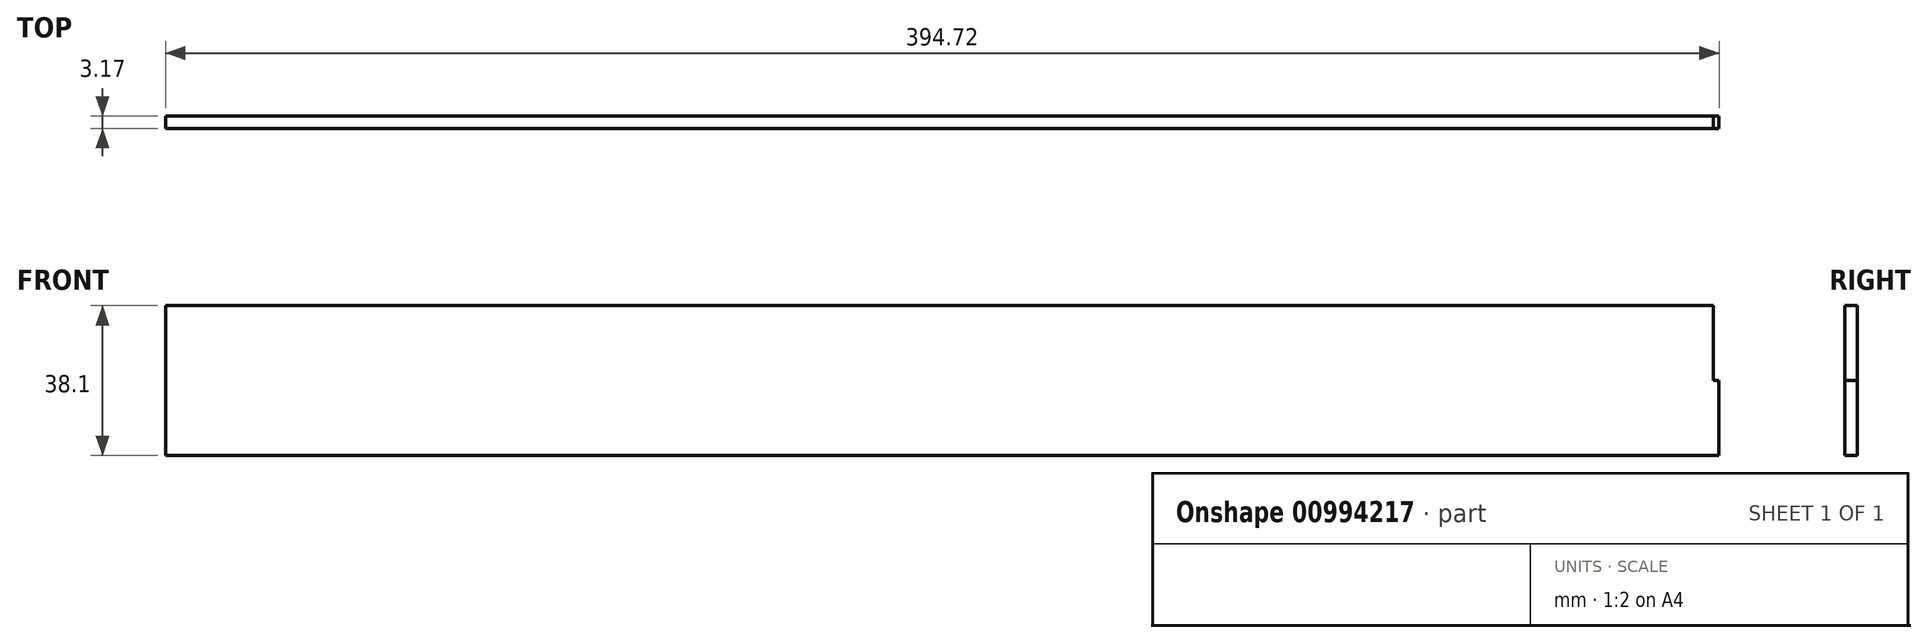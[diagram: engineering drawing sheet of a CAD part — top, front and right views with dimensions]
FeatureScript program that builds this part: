
annotation { "Feature Type Name" : "Feature", "Feature Type Description" : "" }
export const myFeature = defineFeature(function(context is Context, id is Id, definition is map)
    precondition{}
    {
        {
            var Q0;
            Q0=qCreatedBy(makeId("Front.planeOp"),FACE);
            var sketch = newSketch(context, id + "F0", { "sketchPlane" : qUnion([Q0])});
            skLineSegment(sketch, "E0", {"start": v(0, 0) * mm, "end": v(0, 38.1) * mm});
            skLineSegment(sketch, "E1", {"start": v(0, 38.1) * mm, "end": v(393.2, 38.1) * mm});
            skLineSegment(sketch, "E2", {"start": v(393.2, 38.1) * mm, "end": v(393.2, 19.05) * mm});
            skLineSegment(sketch, "E3", {"start": v(0, 0) * mm, "end": v(394.72, 0) * mm});
            skLineSegment(sketch, "E4", {"start": v(394.72, 0) * mm, "end": v(394.72, 19.05) * mm});
            skLineSegment(sketch, "E5", {"start": v(393.2, 19.05) * mm, "end": v(394.72, 19.05) * mm});
            skSolve(sketch);
        }
        {
            var Q0;
            Q0=makeQuery(id+"F0.imprint","IMPRINT",FACE,{"disambiguationData":[TD([[makeQuery(id+"F0.imprint","IMPRINT",EDGE,{"derivedFrom":sQuery(id+"F0.wireOp",EDGE,"E0")}),-1.0]])]});
            extrude(context, id + "F1", {"entities" : qUnion([Q0]), "depth" : 3.17 * mm, "offsetDistance" : 25.4 * mm});
        }
    });
